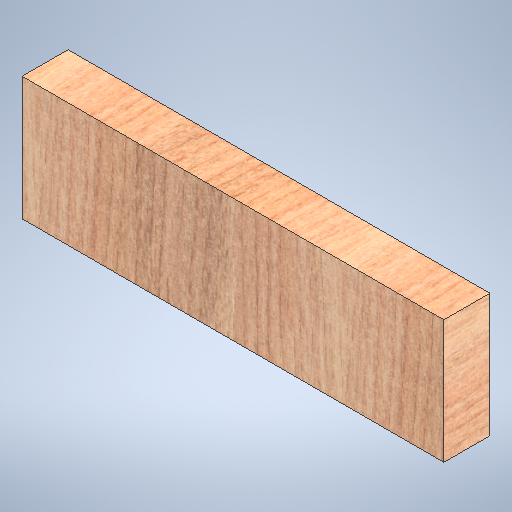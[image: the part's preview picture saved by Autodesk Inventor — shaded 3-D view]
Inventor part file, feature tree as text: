
AUTODESK INVENTOR PART (.ipt)
format: ipt  version: 2025 (Build 290162010, 162A)  size: 435,712 bytes
history: native  units: in
note: dims shown in document units (in); Inventor stores cm internally (conversion verified against a paired STEP export)
features: extrude x1, sketch x1
ambient origin geometry x8: Origin, YZ Plane, XZ Plane, XY Plane, X Axis, Y Axis, Z Axis, Center Point
bodies: Solid1 (feature_tree)
feature tree (2):
  extrude  "Extrusion1"  Depth=13.75in
  sketch  "Sketch1"  dims[d2=4.023in d3=13.75in d4=1.5in d5=0.0in]
